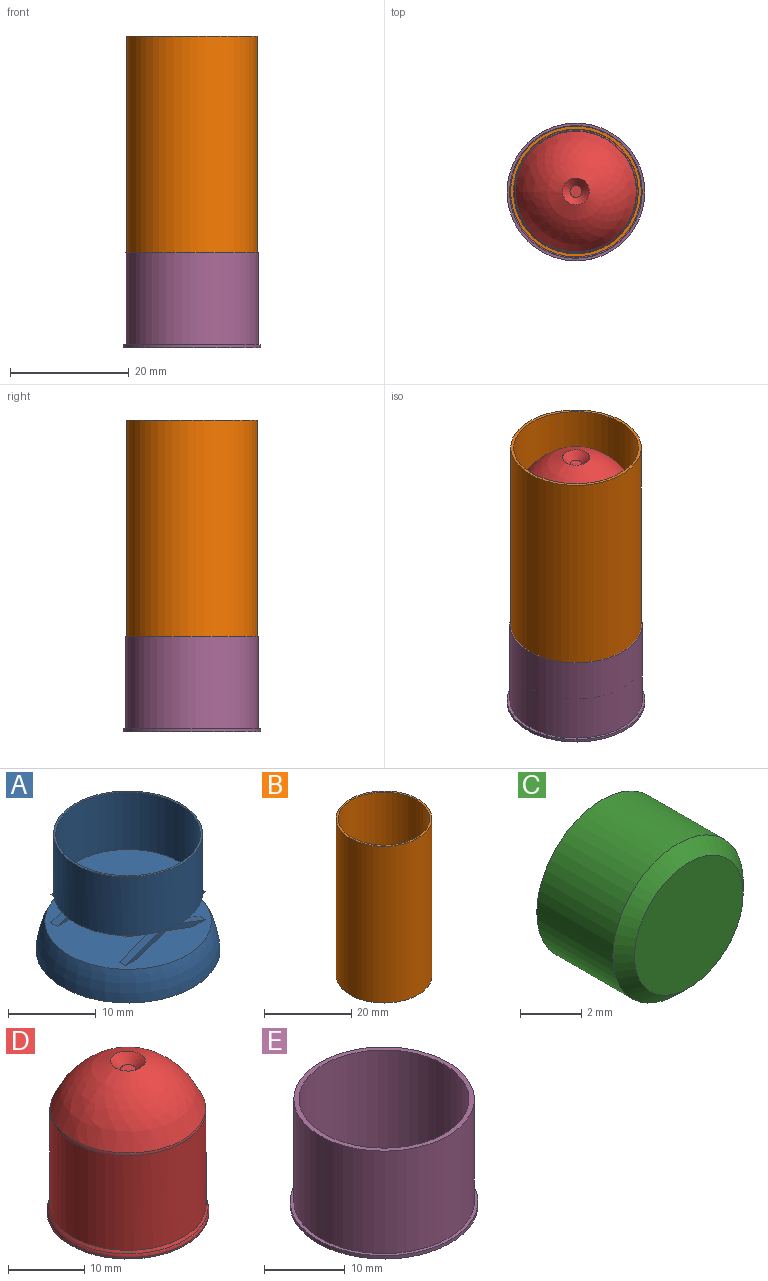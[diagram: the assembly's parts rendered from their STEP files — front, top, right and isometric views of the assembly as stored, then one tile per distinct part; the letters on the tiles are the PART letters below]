
ASSEMBLY  parts=5 mates=4
PART A: 40 faces, bbox 21x21x16.2 mm
  f0: plane 17.01x17.01mm, normal (0,0,-1), area 219.3mm2, adj f1,f6,f7,f8,f9,f10,f11,f12
  f1: cylinder r=8.5mm len=17mm, axis (0,0,1), area 437.9mm2, adj f0,f2,f3,f4,f5,f37
  f2: plane 0.45x0.43mm, normal (0,0,1), area 0.1mm2, adj f1,f8,f21
  f3: plane 0.45x0.43mm, normal (0,0,1), area 0.1mm2, adj f1,f8,f18
  f4: plane 0.46x0.43mm, normal (0,0,1), area 0.1mm2, adj f1,f12,f25
  f5: plane 0.45x0.43mm, normal (0,0,1), area 0.1mm2, adj f1,f12,f26
  f6: plane 4.43x1.63mm, normal (0.34,0,0.94), area 4.7mm2, adj f0,f7,f8,f9
  f7: plane 4.43x1.63mm, normal (-0.34,0,0.94), area 4.7mm2, adj f0,f6,f8,f9
  f8: plane 12.89x4mm, normal (0,1,0), area 15.2mm2, adj f0,f2,f3,f6,f7,f14,f17,f18
  f9: plane 12.9x4mm, normal (0,-1,0), area 14.8mm2, adj f0,f6,f7,f14,f17,f18,f19,f20
  f10: plane 4.43x1.63mm, normal (-0.34,0,0.94), area 4.7mm2, adj f0,f11,f12,f13
  f11: plane 4.43x1.63mm, normal (0.34,0,0.94), area 4.7mm2, adj f0,f10,f12,f13
  f12: plane 12.89x4mm, normal (0,-1,0), area 15.2mm2, adj f0,f4,f5,f10,f11,f14,f25,f26
  f13: plane 12.89x4mm, normal (0,1,0), area 14.8mm2, adj f0,f10,f11,f14,f25,f26,f27,f28
  f14: plane 19x18.95mm, normal (0,0,1), area 275.5mm2, adj f8,f9,f12,f13,f16,f17,f19,f20
  f15: plane 21x21mm, normal (0,0,-1), area 77.5mm2, adj f16,f23,f24,f35
  f16: torus R=0.21mm, axis (0,0,1), area 264.3mm2, adj f14,f15,f24
  f17: plane 5.45x2mm, normal (-0.34,0,0.94), area 5.8mm2, adj f8,f9,f14,f18
  f18: plane 5.46x2.01mm, normal (-0.34,0,-0.94), area 5.8mm2, adj f0,f3,f8,f9,f17
  f19: plane 4.45x1.63mm, normal (-0.34,0,-0.94), area 4.7mm2, adj f8,f9,f14,f20
  f20: plane 4.45x1.63mm, normal (0.34,0,-0.94), area 4.7mm2, adj f8,f9,f14,f19
  f21: plane 5.45x2mm, normal (0.34,0,-0.94), area 5.8mm2, adj f0,f2,f8,f9,f22
  f22: plane 5.45x2mm, normal (0.34,0,0.94), area 5.8mm2, adj f8,f9,f14,f21
  f23: plane 4x2mm, normal (1,0,0), area 8mm2, adj f14,f15,f24
  f24: cylinder r=9.5mm len=4mm, axis (0,0,1), area 8mm2, adj f15,f16,f23
  f25: plane 5.46x2.01mm, normal (0.34,0,-0.94), area 5.8mm2, adj f0,f4,f12,f13,f30
  f26: plane 5.45x2mm, normal (-0.34,0,-0.94), area 5.8mm2, adj f0,f5,f12,f13,f27
  f27: plane 5.45x2mm, normal (-0.34,0,0.94), area 5.8mm2, adj f12,f13,f14,f26
  f28: plane 4.45x1.63mm, normal (0.34,0,-0.94), area 4.7mm2, adj f12,f13,f14,f29
  f29: plane 4.45x1.63mm, normal (-0.34,0,-0.94), area 4.7mm2, adj f12,f13,f14,f28
  f30: plane 5.45x2mm, normal (0.34,0,0.94), area 5.8mm2, adj f12,f13,f14,f25
  f31: plane 10x1.01mm, normal (0,0,-1), area 10.1mm2, adj f9,f13,f32,f34
  f32: plane 10x0.45mm, normal (1,0,0), area 4.5mm2, adj f9,f13,f31,f33
  f33: plane 10x1.01mm, normal (0,0,1), area 10.1mm2, adj f9,f13,f32,f34
  f34: plane 10x0.45mm, normal (-1,0,0), area 4.5mm2, adj f9,f13,f31,f33
  f35: cylinder r=9.25mm len=18.5mm, axis (0,0,-1), area 116.2mm2, adj f15,f36
  f36: plane 18.5x18.5mm, normal (0,0,-1), area 268.8mm2, adj f35
  f37: plane 17x17mm, normal (0,0,1), area 13.2mm2, adj f1,f38
  f38: cylinder r=8.25mm len=16.5mm, axis (0,0,1), area 414.7mm2, adj f37,f39
  f39: plane 16.5x16.5mm, normal (0,0,1), area 213.8mm2, adj f38
PART B: 4 faces, bbox 22x22x44 mm
  f0: cylinder r=11mm len=44mm, axis (0,0,-1), area 3041.1mm2, adj f1,f2
  f1: plane 22x22mm, normal (0,0,1), area 33.8mm2, adj f0,f3
  f2: plane 22x22mm, normal (0,0,-1), area 33.8mm2, adj f0,f3
  f3: cylinder r=10.5mm len=44mm, axis (0,0,1), area 2902.8mm2, adj f1,f2
PART C: 4 faces, bbox 6x4x6 mm
  f0: cylinder r=3mm len=6mm, axis (0,1,0), area 66mm2, adj f2,f3
  f1: plane 5x5mm, normal (0,-1,0), area 19.6mm2, adj f2
  f2: cone r=2.5mm half-angle=45deg, axis (0,1,0), area 12.2mm2, adj f0,f1
  f3: plane 6x6mm, normal (0,1,0), area 28.3mm2, adj f0
PART D: 9 faces, bbox 22.9x22.9x24.3 mm
  f0: plane 21.2x21.2mm, normal (0,0,-1), area 353mm2, adj f1
  f1: cylinder r=10.6mm len=21.2mm, axis (0,0,-1), area 15.5mm2, adj f0,f5
  f2: cone r=10.6mm half-angle=30deg, axis (0,0,-1), area 30.2mm2, adj f3,f5
  f3: cylinder r=10.23mm len=20.47mm, axis (0,0,-1), area 978.3mm2, adj f2,f6
  f4: revolved ~20.34x20.34mm, area 481.3mm2, adj f6,f8
  f5: torus R=9.6mm, axis (0,0,1), area 34.7mm2, adj f1,f2
  f6: torus R=9.23mm, axis (0,0,1), area 23.5mm2, adj f3,f4
  f7: plane 2x2mm, normal (0,0,1), area 3.1mm2, adj f8
  f8: cone r=3mm half-angle=45deg, axis (0,0,1), area 18.4mm2, adj f4,f7
PART E: 8 faces, bbox 23.2x23.2x16 mm
  f0: plane 23.2x23.2mm, normal (0,0,-1), area 372.5mm2, adj f1,f7
  f1: cylinder r=11.6mm len=23.2mm, axis (0,0,1), area 36.4mm2, adj f0,f2
  f2: plane 23.2x23.2mm, normal (0,0,1), area 32.2mm2, adj f1,f3
  f3: cylinder r=11.15mm len=22.3mm, axis (0,0,1), area 1085.9mm2, adj f2,f4
  f4: plane 22.3x22.3mm, normal (0,0,1), area 44.2mm2, adj f3,f5
  f5: cylinder r=10.5mm len=21mm, axis (0,0,1), area 989.6mm2, adj f4,f6
  f6: plane 21x21mm, normal (0,0,1), area 318.1mm2, adj f5,f7
  f7: torus R=4mm, axis (0,0,1), area 33.2mm2, adj f0,f6
PLACE A t=(-7.2,-8.1,-0.92)mm
PLACE B rot(axis=(1,0,0),180deg) t=(-7.2,-8.1,38.58)mm
PLACE C rot(axis=(-1,0,0),90deg) t=(-7.2,-8.1,-10.62)mm
PLACE D t=(-7.2,-8.1,22.38)mm
PLACE E t=(-7.2,-8.1,5.39)mm
MATE fastened D.f1 <-> A.f38  axis (0,0,-1) through (-7.2,-8.1,12.28)mm
MATE fastened B.f3 <-> E.f5  axis (0,0,-1) through (-7.2,-8.1,-5.42)mm
MATE fastened A.f35 <-> E.f5  axis (0,0,-1) through (-7.2,-8.1,-4.92)mm
MATE fastened C.f0 <-> E.f7  axis (0,0,-1) through (-7.2,-8.1,-13.62)mm
